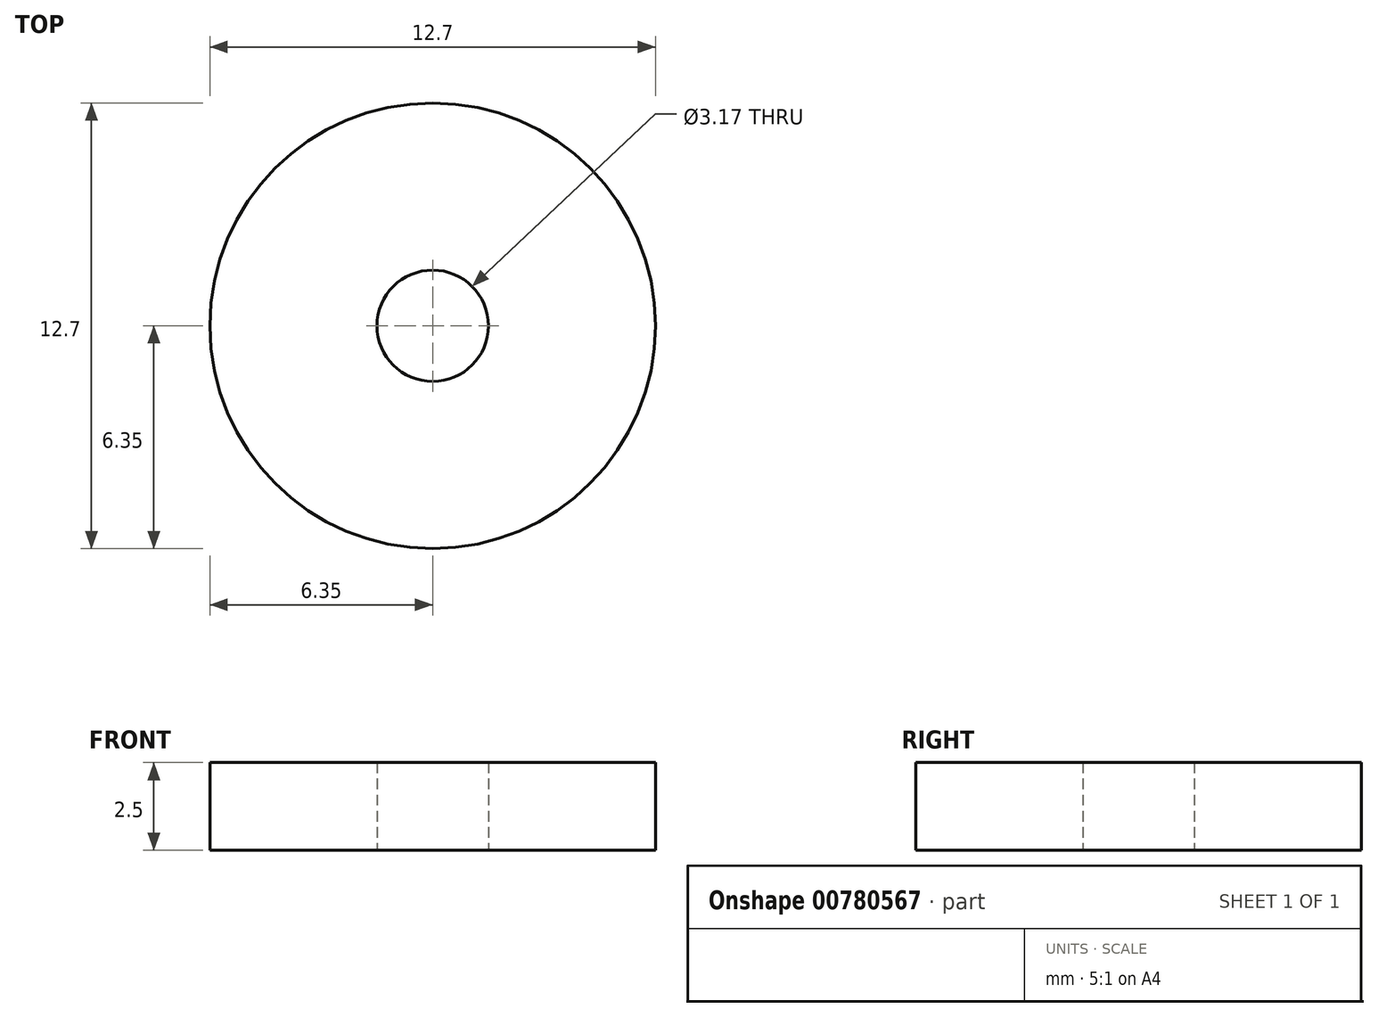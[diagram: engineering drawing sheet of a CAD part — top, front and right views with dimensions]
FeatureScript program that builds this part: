
annotation { "Feature Type Name" : "Feature", "Feature Type Description" : "" }
export const myFeature = defineFeature(function(context is Context, id is Id, definition is map)
    precondition{}
    {
        {
            var Q0;
            Q0=qCreatedBy(makeId("Top.planeOp"),FACE);
            var sketch = newSketch(context, id + "F0", { "sketchPlane" : qUnion([Q0])});
            skCircle(sketch, "E0", {"center": v(0, 0) * mm, "radius": 6.35 * mm});
            skCircle(sketch, "E1", {"center": v(0, 0) * mm, "radius": 1.59 * mm});
            skSolve(sketch);
        }
        {
            var Q0;
            Q0=makeQuery(id+"F0.imprint","IMPRINT",FACE,{"disambiguationData":[TD([[makeQuery(id+"F0.imprint","IMPRINT",EDGE,{"derivedFrom":sQuery(id+"F0.wireOp",EDGE,"E0")}),1.0]])]});
            extrude(context, id + "F1", {"entities" : qUnion([Q0]), "depth" : 2.5 * mm, "offsetDistance" : 25.4 * mm});
        }
    });
